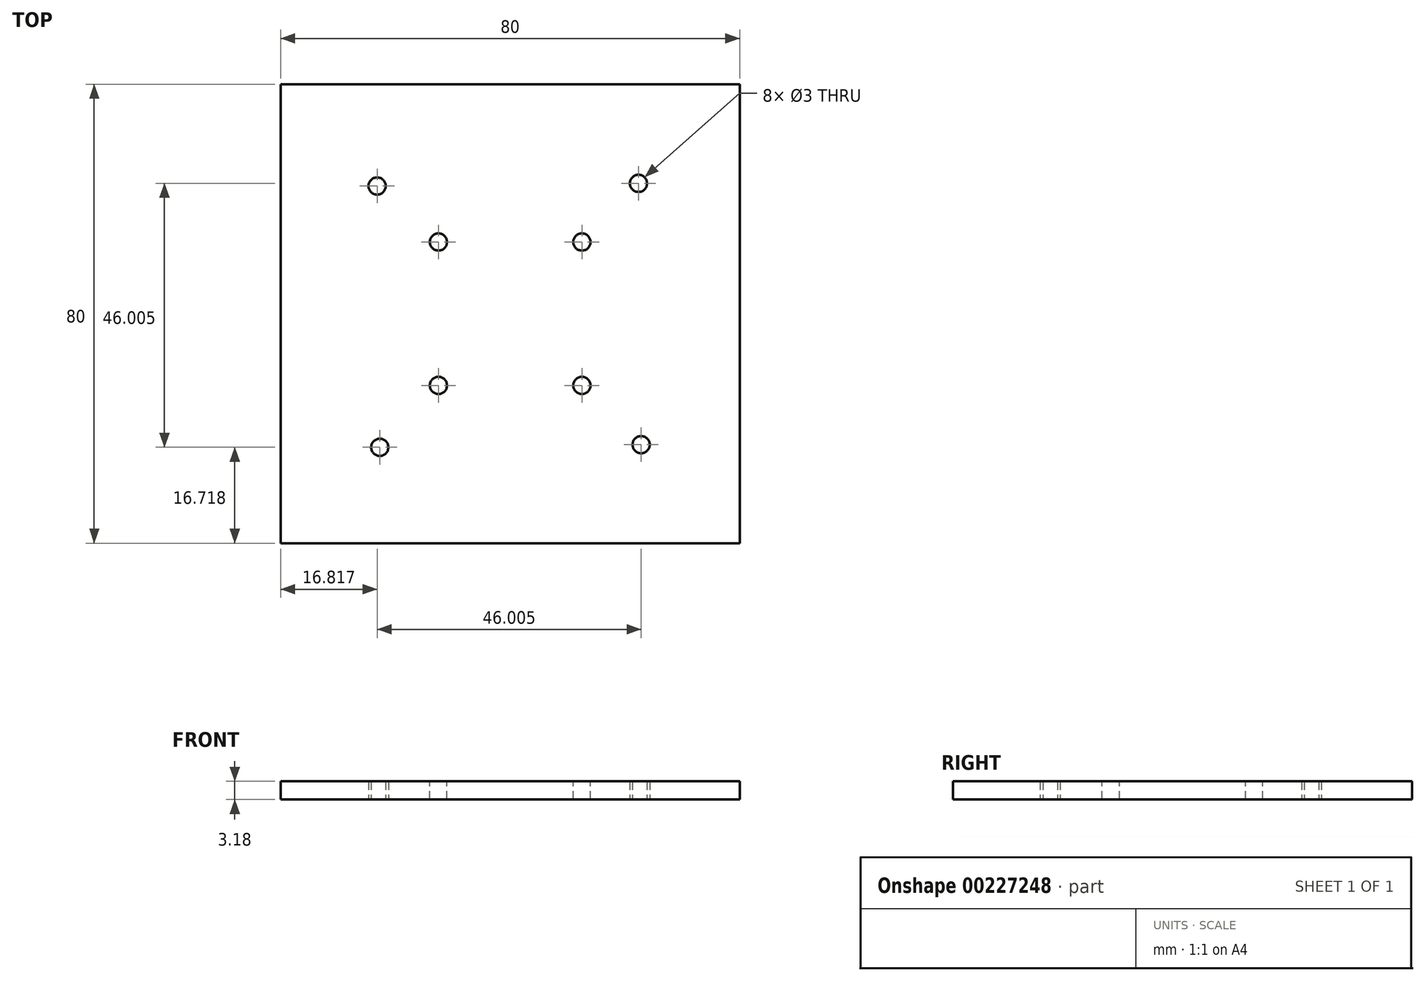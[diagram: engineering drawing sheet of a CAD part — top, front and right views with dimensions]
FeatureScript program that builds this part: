
annotation { "Feature Type Name" : "Feature", "Feature Type Description" : "" }
export const myFeature = defineFeature(function(context is Context, id is Id, definition is map)
    precondition{}
    {
        {
            var Q0;
            Q0=qCreatedBy(makeId("Top.planeOp"),FACE);
            var sketch = newSketch(context, id + "F0", { "sketchPlane" : qUnion([Q0])});
            skLineSegment(sketch, "E0.bottom", {"start": v(40, -40) * mm, "end": v(-40, -40) * mm});
            skLineSegment(sketch, "E0.top", {"start": v(40, 40) * mm, "end": v(-40, 40) * mm});
            skLineSegment(sketch, "E0.left", {"start": v(40, -40) * mm, "end": v(40, 40) * mm});
            skLineSegment(sketch, "E0.right", {"start": v(-40, -40) * mm, "end": v(-40, 40) * mm});
            skCircle(sketch, "E1", {"center": v(-23.18, 22.26) * mm, "radius": 1.5 * mm});
            skCircle(sketch, "E2.1.0", {"center": v(-22.72, -23.28) * mm, "radius": 1.5 * mm});
            skCircle(sketch, "E2.2.0", {"center": v(22.82, -22.82) * mm, "radius": 1.5 * mm});
            skCircle(sketch, "E2.3.0", {"center": v(22.36, 22.72) * mm, "radius": 1.5 * mm});
            skPoint(sketch, "E2.center", {"position": v(-0.18, -0.28) * mm});
            skSolve(sketch);
        }
        {
            var Q0;
            Q0 = qSketchRegion(id + "F0", true);
            extrude(context, id + "F1", {"entities" : qUnion([Q0]), "depth" : 3.17 * mm});
        }
        {
            var Q0;
            Q0=makeQuery(id+"F1.opExtrude","CAP_FACE",FACE,{"disambiguationData":[OSD([sQuery(id+"F0.wireOp",EDGE,"E0.bottom"),sQuery(id+"F0.wireOp",EDGE,"E0.top"),sQuery(id+"F0.wireOp",EDGE,"E0.left"),sQuery(id+"F0.wireOp",EDGE,"E0.right"),sQuery(id+"F0.wireOp",EDGE,"E1"),sQuery(id+"F0.wireOp",EDGE,"E2.1.0"),sQuery(id+"F0.wireOp",EDGE,"E2.2.0"),sQuery(id+"F0.wireOp",EDGE,"E2.3.0")])],"isStart":false});
            var sketch = newSketch(context, id + "F2", { "sketchPlane" : qUnion([Q0])});
            skCircle(sketch, "E3.cCircle", {"center": v(0, 0) * mm, "radius": 17.68 * mm, "construction": true});
            skLineSegment(sketch, "E3.0", {"start": v(12.5, -12.5) * mm, "end": v(-12.5, -12.5) * mm, "construction": true});
            skLineSegment(sketch, "E3.1", {"start": v(-12.5, -12.5) * mm, "end": v(-12.5, 12.5) * mm, "construction": true});
            skLineSegment(sketch, "E3.2", {"start": v(-12.5, 12.5) * mm, "end": v(12.5, 12.5) * mm, "construction": true});
            skLineSegment(sketch, "E3.3", {"start": v(12.5, 12.5) * mm, "end": v(12.5, -12.5) * mm, "construction": true});
            skCircle(sketch, "E4", {"center": v(-12.5, 12.5) * mm, "radius": 1.5 * mm});
            skCircle(sketch, "E5.1.0", {"center": v(-12.5, -12.5) * mm, "radius": 1.5 * mm});
            skCircle(sketch, "E5.2.0", {"center": v(12.5, -12.5) * mm, "radius": 1.5 * mm});
            skCircle(sketch, "E5.3.0", {"center": v(12.5, 12.5) * mm, "radius": 1.5 * mm});
            skSolve(sketch);
        }
        {
            var Q0;
            Q0=makeQuery(id+"F2.imprint","IMPRINT",FACE,{"disambiguationData":[TD([[makeQuery(id+"F2.imprint","IMPRINT",EDGE,{"derivedFrom":sQuery(id+"F2.wireOp",EDGE,"E4")}),1.0]])]});
            var Q1;
            Q1=makeQuery(id+"F2.imprint","IMPRINT",FACE,{"disambiguationData":[TD([[makeQuery(id+"F2.imprint","IMPRINT",EDGE,{"derivedFrom":sQuery(id+"F2.wireOp",EDGE,"E5.3.0")}),1.0]])]});
            var Q2;
            Q2=makeQuery(id+"F2.imprint","IMPRINT",FACE,{"disambiguationData":[TD([[makeQuery(id+"F2.imprint","IMPRINT",EDGE,{"derivedFrom":sQuery(id+"F2.wireOp",EDGE,"E5.2.0")}),1.0]])]});
            var Q3;
            Q3=makeQuery(id+"F2.imprint","IMPRINT",FACE,{"disambiguationData":[TD([[makeQuery(id+"F2.imprint","IMPRINT",EDGE,{"derivedFrom":sQuery(id+"F2.wireOp",EDGE,"E5.1.0")}),1.0]])]});
            var Q4;
            Q4=sQuery(id+"F2.wireOp",EDGE,"E4");
            var Q5;
            Q5=sQuery(id+"F2.wireOp",EDGE,"E5.3.0");
            var Q6;
            Q6=sQuery(id+"F2.wireOp",EDGE,"E5.2.0");
            var Q7;
            Q7=sQuery(id+"F2.wireOp",EDGE,"E5.1.0");
            extrude(context, id + "F3", {"entities" : qUnion([Q0, Q1, Q2, Q3]), "operationType" : NewBodyOperationType.REMOVE, "surfaceEntities" : qUnion([Q4, Q5, Q6, Q7]), "oppositeDirection" : true, "depth" : 25 * mm});
        }
    });
